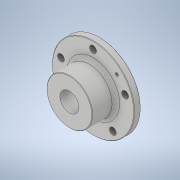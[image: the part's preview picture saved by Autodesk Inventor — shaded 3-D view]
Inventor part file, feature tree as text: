
AUTODESK INVENTOR PART (.ipt)
format: ipt  version: 2021 (Build 250183000, 183)  size: 219,648 bytes
history: native  units: in
note: dims shown in document units (in); Inventor stores cm internally (conversion verified against a paired STEP export)
features: thread x6, sketch x4, extrude x3, fillet x2, revolve x1, chamfer x1
ambient origin geometry x8: Origin, YZ Plane, XZ Plane, XY Plane, X Axis, Y Axis, Z Axis, Center Point
bodies: Solid1 (feature_tree)
feature tree (17):
  revolve  "Revolution1"  [1 undecoded]
  extrude  "Extrusion1"  Depth=0.435in
  extrude  "Extrusion2"  Depth=0.2in
  fillet  "Fillet1"  Radius=0.16in
  chamfer  "Chamfer1"  Angle=90.0deg  [1 undecoded]
  fillet  "Fillet2"  Radius=2.0in
  extrude  "Extrusion3"  Depth=1.0in TaperAngle=0.0deg
  thread  "Thread1"  [1 undecoded]
  thread  "Thread2"  [1 undecoded]
  thread  "Thread3"  [1 undecoded]
  thread  "Thread4"  [1 undecoded]
  thread  "Thread5"  [1 undecoded]
  thread  "Thread6"  [1 undecoded]
  sketch  "Sketch1"  dims[d0=1.5in d1=1.56in]
  sketch  "Sketch2"  dims[d2=1.2in d3=0.435in]
  sketch  "Sketch3"  dims[d4=1.42in d5=0.2in d6=0.16in]
  sketch  "Sketch4"  dims[d7=0.52in d8=90.0deg d9=2.0in d10=1.0in d11=0.0in d12=1.25in d13=1.0in d14=0.0in d15=0.075in d16=0.03in d17=0.125in d18=45.0deg d19=0.25in d20=0.452in d21=0.48in d22=1.9685in d24=360.0deg d26=45.0deg d27=0.2in d28=0.2in d29=0.0in d30=0.435in d31=0.0in d32=0.435in d33=0.0in d34=0.435in d35=0.0in d36=0.435in d37=0.0in d38=0.435in d39=0.0in d40=0.435in d41=0.0in]
note: 8 required parameter values undecoded (feature->parameter linkage not recoverable at this tier; creation-order binding heuristic only, values carry confidence <= 0.55)